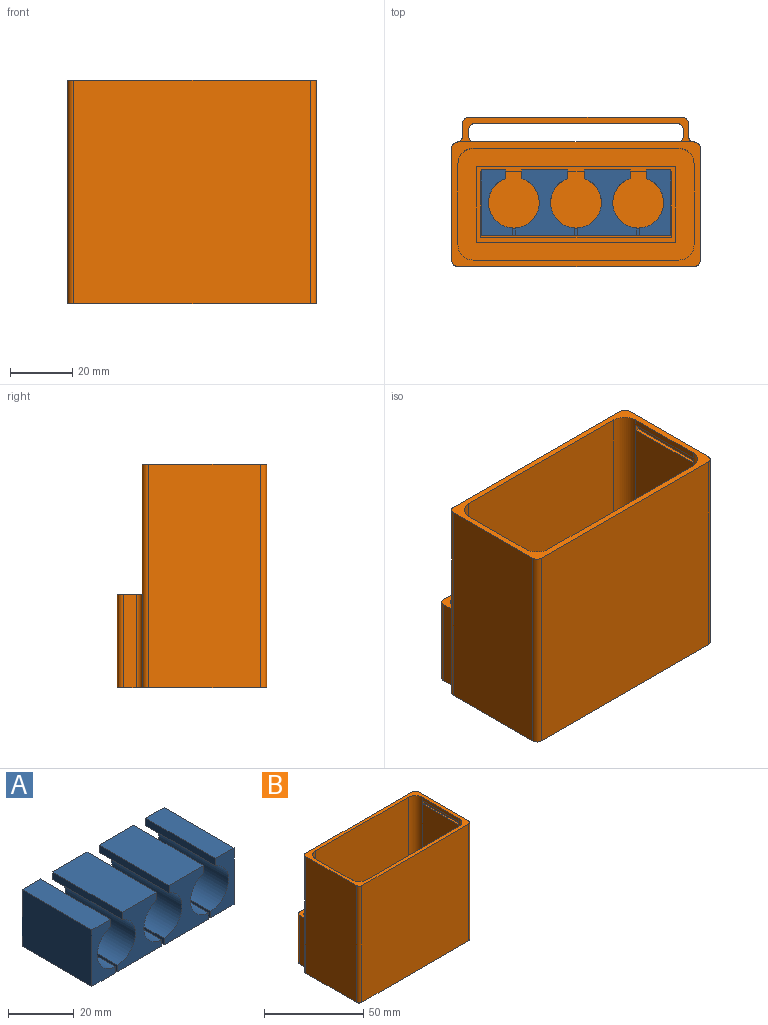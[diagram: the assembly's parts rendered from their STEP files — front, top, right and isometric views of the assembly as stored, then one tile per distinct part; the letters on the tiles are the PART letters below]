
ASSEMBLY  parts=2 mates=1
PART A: 30 faces, bbox 61x30x21 mm
  f0: cylinder r=8.18mm len=30mm, axis (0,1,0), area 1362.2mm2, adj f1,f4,f5,f19,f20,f27,f28,f29
  f1: plane 21x19mm, normal (0,-1,0), area 194.9mm2, adj f0,f4,f8,f16,f17,f18,f21,f27
  f2: plane 21x19mm, normal (0,-1,0), area 194.9mm2, adj f8,f12,f13,f14,f15,f16,f22,f24
  f3: plane 21x10mm, normal (0,-1,0), area 107.9mm2, adj f8,f9,f10,f11,f12,f25
  f4: plane 30x2.75mm, normal (-1,0,0), area 82.5mm2, adj f0,f1,f18,f20
  f5: plane 30x2.75mm, normal (1,0,0), area 82.5mm2, adj f0,f6,f19,f20
  f6: plane 30x7.9mm, normal (0,0,1), area 237mm2, adj f5,f7,f19,f20
  f7: plane 30x21mm, normal (-1,0,0), area 630mm2, adj f6,f8,f19,f20
  f8: plane 61x30mm, normal (0,0,-1), area 1770mm2, adj f1,f2,f3,f7,f9,f19,f20,f21
  f9: plane 30x21mm, normal (1,0,0), area 630mm2, adj f3,f8,f10,f20
  f10: plane 30x7.9mm, normal (0,0,1), area 237mm2, adj f3,f9,f11,f20
  f11: plane 30x2.75mm, normal (-1,0,0), area 82.5mm2, adj f3,f10,f12,f20
  f12: cylinder r=8.18mm len=30mm, axis (0,1,0), area 1362.2mm2, adj f2,f3,f11,f13,f20,f24,f25,f26
  f13: plane 30x2.75mm, normal (1,0,0), area 82.5mm2, adj f2,f12,f14,f20
  f14: plane 30x14.8mm, normal (0,0,1), area 444mm2, adj f2,f13,f15,f20
  f15: plane 30x2.75mm, normal (-1,0,0), area 82.5mm2, adj f2,f14,f16,f20
  f16: cylinder r=8.18mm len=30mm, axis (0,1,0), area 1362.2mm2, adj f1,f2,f15,f17,f20,f21,f22,f23
  f17: plane 30x2.75mm, normal (1,0,0), area 82.5mm2, adj f1,f16,f18,f20
  f18: plane 30x14.8mm, normal (0,0,1), area 444mm2, adj f1,f4,f17,f20
  f19: plane 21x10mm, normal (0,-1,0), area 107.9mm2, adj f0,f5,f6,f7,f8,f28
  f20: plane 61x21mm, normal (0,1,0), area 612.7mm2, adj f0,f4,f5,f6,f7,f8,f9,f10
  f21: plane 20x2.34mm, normal (1,0,0), area 46.8mm2, adj f1,f8,f16,f23
  f22: plane 20x2.34mm, normal (-1,0,0), area 46.8mm2, adj f2,f8,f16,f23
  f23: plane 2.34x1mm, normal (0,-1,0), area 2.3mm2, adj f8,f16,f21,f22
  f24: plane 20x2.34mm, normal (1,0,0), area 46.8mm2, adj f2,f8,f12,f26
  f25: plane 20x2.34mm, normal (-1,0,0), area 46.8mm2, adj f3,f8,f12,f26
  f26: plane 2.34x1mm, normal (0,-1,0), area 2.3mm2, adj f8,f12,f24,f25
  f27: plane 20x2.34mm, normal (-1,0,0), area 46.8mm2, adj f0,f1,f8,f29
  f28: plane 20x2.34mm, normal (1,0,0), area 46.8mm2, adj f0,f8,f19,f29
  f29: plane 2.34x1mm, normal (0,-1,0), area 2.3mm2, adj f0,f8,f27,f28
PART B: 56 faces, bbox 80x48x72 mm
  f0: plane 76x36mm, normal (0,0,1), area 1160.9mm2, adj f2,f6,f7,f9,f13,f14,f15,f16
  f1: plane 26x2mm, normal (1,0,0), area 52mm2, adj f11,f13,f16,f29
  f2: plane 66x26mm, normal (-1,0,0), area 1716mm2, adj f0,f14,f15,f22
  f3: plane 76x72mm, normal (0,1,0), area 5142.2mm2, adj f11,f12,f17,f20,f37,f49,f54
  f4: plane 72x36mm, normal (-1,0,0), area 2592mm2, adj f11,f12,f17,f18
  f5: plane 76x72mm, normal (0,-1,0), area 5472mm2, adj f11,f12,f18,f19
  f6: plane 66x26mm, normal (1,0,0), area 1716mm2, adj f0,f13,f16,f27
  f7: plane 70x66mm, normal (0,-1,0), area 4620mm2, adj f0,f11,f13,f14
  f8: plane 26x2mm, normal (-1,0,0), area 52mm2, adj f11,f14,f15,f24
  f9: plane 70x66mm, normal (0,1,0), area 4620mm2, adj f0,f11,f15,f16
  f10: plane 72x36mm, normal (1,0,0), area 2592mm2, adj f11,f12,f19,f20
  f11: plane 80x40mm, normal (0,0,1), area 482mm2, adj f1,f3,f4,f5,f7,f8,f9,f10
  f12: plane 80x48mm, normal (0,0,-1), area 3367.4mm2, adj f3,f4,f5,f10,f17,f18,f19,f20
  f13: cylinder r=5mm len=70mm, axis (0,0,-1), area 549.8mm2, adj f0,f1,f6,f7,f11,f28
  f14: cylinder r=5mm len=70mm, axis (0,0,1), area 549.8mm2, adj f0,f2,f7,f8,f11,f21
  f15: cylinder r=5mm len=70mm, axis (0,0,-1), area 549.8mm2, adj f0,f2,f8,f9,f11,f23
  f16: cylinder r=5mm len=70mm, axis (0,0,1), area 549.8mm2, adj f0,f1,f6,f9,f11,f26
  f17: cylinder r=2mm len=72mm, axis (0,0,1), area 218.5mm2, adj f3,f4,f11,f12,f37,f50
  f18: cylinder r=2mm len=72mm, axis (0,0,-1), area 226.2mm2, adj f4,f5,f11,f12
  f19: cylinder r=2mm len=72mm, axis (0,0,1), area 226.2mm2, adj f5,f10,f11,f12
  f20: cylinder r=2mm len=72mm, axis (0,0,-1), area 223.6mm2, adj f3,f10,f11,f12,f37,f53
  f21: plane 2x1mm, normal (0,-1,0), area 2mm2, adj f14,f22,f24,f25
  f22: plane 26x1mm, normal (0,0,1), area 26mm2, adj f2,f21,f23,f25
  f23: plane 2x1mm, normal (0,1,0), area 2mm2, adj f15,f22,f24,f25
  f24: plane 26x1mm, normal (0,0,-1), area 26mm2, adj f8,f21,f23,f25
  f25: plane 26x2mm, normal (-1,0,0), area 52mm2, adj f21,f22,f23,f24
  f26: plane 2x1mm, normal (0,1,0), area 2mm2, adj f16,f27,f29,f30
  f27: plane 26x1mm, normal (0,0,1), area 26mm2, adj f6,f26,f28,f30
  f28: plane 2x1mm, normal (0,-1,0), area 2mm2, adj f13,f27,f29,f30
  f29: plane 26x1mm, normal (0,0,-1), area 26mm2, adj f1,f26,f28,f30
  f30: plane 26x2mm, normal (1,0,0), area 52mm2, adj f26,f27,f28,f29
  f31: plane 65.01x30mm, normal (0,-1,0), area 1950.2mm2, adj f12,f37,f48,f55
  f32: plane 30x2mm, normal (1,0,0), area 60mm2, adj f12,f37,f48,f49
  f33: plane 30x4.03mm, normal (-1,0,0), area 121mm2, adj f12,f37,f50,f51
  f34: plane 68.69x30mm, normal (0,1,0), area 2060.6mm2, adj f12,f37,f51,f52
  f35: plane 30x4mm, normal (1,0,0), area 120.1mm2, adj f12,f37,f52,f53
  f36: plane 30x2mm, normal (-1,0,0), area 60mm2, adj f12,f37,f54,f55
  f37: plane 76.34x8.02mm, normal (0,0,1), area 170.8mm2, adj f3,f17,f20,f31,f32,f33,f34,f35
  f38: plane 24.2x2mm, normal (-1,0,0), area 48.4mm2, adj f0,f39,f45,f46
  f39: plane 64.2x2mm, normal (0,-1,0), area 128.4mm2, adj f0,f38,f40,f46
  f40: plane 24.2x2mm, normal (1,0,0), area 48.4mm2, adj f0,f39,f45,f46
  f41: plane 61.2x2mm, normal (0,1,0), area 122.4mm2, adj f42,f44,f46,f47
  f42: plane 21.2x2mm, normal (1,0,0), area 42.4mm2, adj f41,f43,f46,f47
  f43: plane 61.2x2mm, normal (0,-1,0), area 122.4mm2, adj f42,f44,f46,f47
  f44: plane 21.2x2mm, normal (-1,0,0), area 42.4mm2, adj f41,f43,f46,f47
  f45: plane 64.2x2mm, normal (0,1,0), area 128.4mm2, adj f0,f38,f40,f46
  f46: plane 64.2x24.2mm, normal (0,0,1), area 256.2mm2, adj f38,f39,f40,f41,f42,f43,f44,f45
  f47: plane 61.2x21.2mm, normal (0,0,1), area 1297.4mm2, adj f41,f42,f43,f44
  f48: cylinder r=2mm len=30mm, axis (0,0,1), area 94.2mm2, adj f12,f31,f32,f37
  f49: cylinder r=2mm len=30mm, axis (0,0,1), area 94.2mm2, adj f3,f12,f32,f37
  f50: cylinder r=2mm len=30mm, axis (0,0,1), area 86.5mm2, adj f12,f17,f33,f37
  f51: cylinder r=2mm len=30mm, axis (0,0,-1), area 94.2mm2, adj f12,f33,f34,f37
  f52: cylinder r=2mm len=30mm, axis (0,0,-1), area 94.2mm2, adj f12,f34,f35,f37
  f53: cylinder r=2mm len=30mm, axis (0,0,-1), area 91.7mm2, adj f12,f20,f35,f37
  f54: cylinder r=2mm len=30mm, axis (0,0,1), area 94.2mm2, adj f3,f12,f36,f37
  f55: cylinder r=2mm len=30mm, axis (0,0,1), area 94.2mm2, adj f12,f31,f36,f37
PLACE A rot(axis=(-1,0,0),90deg) t=(48.94,-67.26,-73.78)mm
PLACE B rot(axis=(-0.31,0.33,-0.89),0deg) t=(46.33,-71.41,-73.78)mm
MATE planar B.f47 <-> A.f20  axis (0,0,1) through (31.87,-55.12,-73.78)mm
